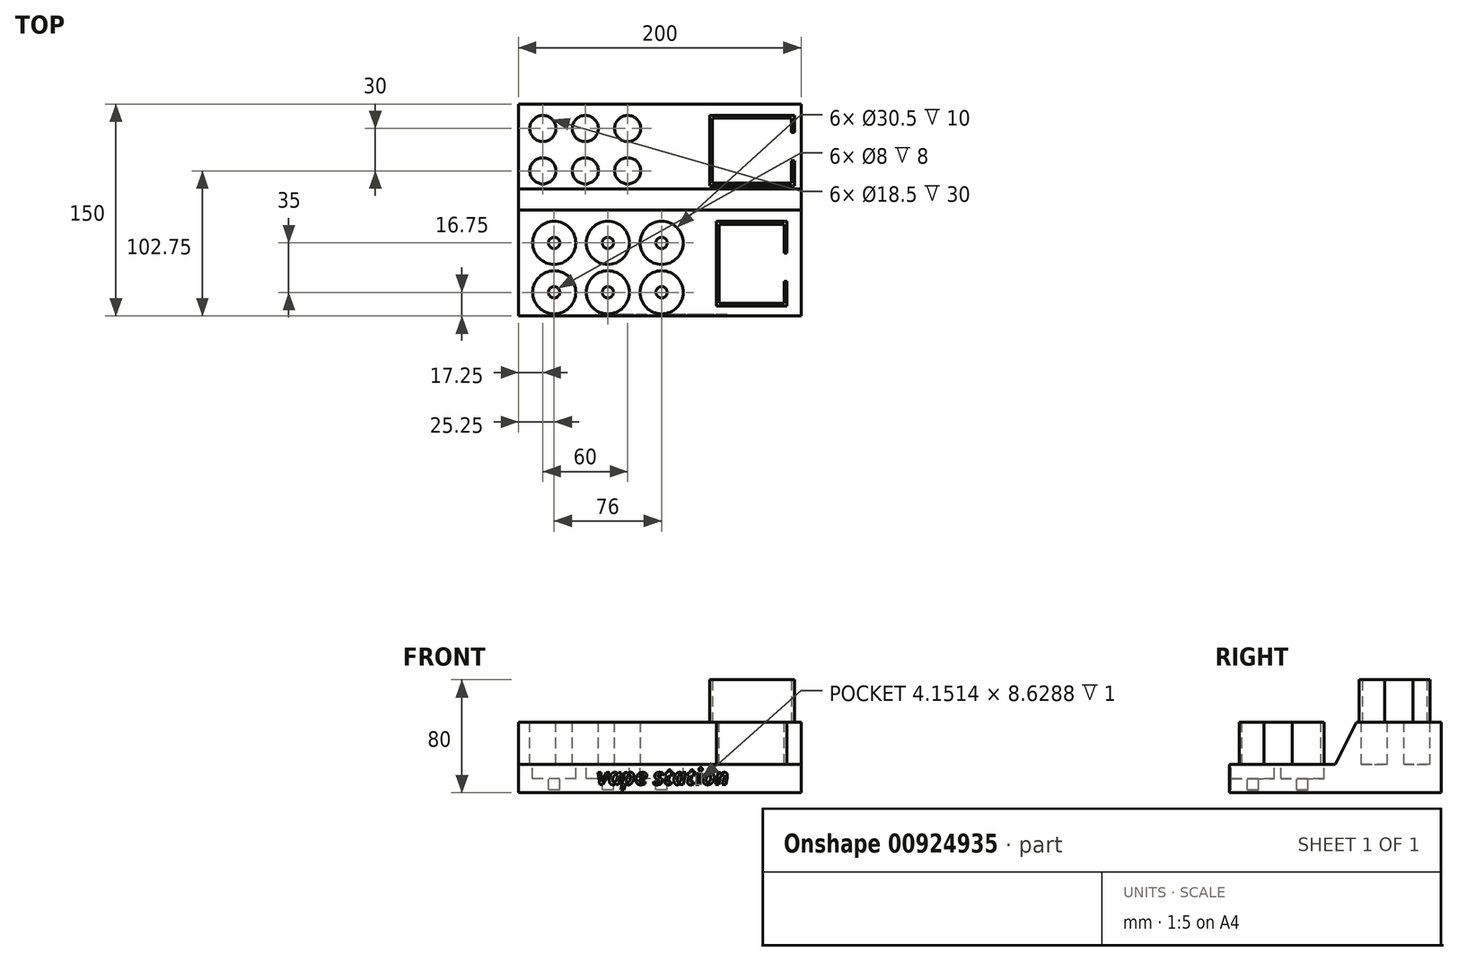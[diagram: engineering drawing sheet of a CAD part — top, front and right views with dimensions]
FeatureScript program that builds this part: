
annotation { "Feature Type Name" : "Feature", "Feature Type Description" : "" }
export const myFeature = defineFeature(function(context is Context, id is Id, definition is map)
    precondition{}
    {
        {
            var Q0;
            Q0=qCreatedBy(makeId("Top.planeOp"),FACE);
            var sketch = newSketch(context, id + "F0", { "sketchPlane" : qUnion([Q0])});
            skLineSegment(sketch, "E0.bottom", {"start": v(100, -75) * mm, "end": v(-100, -75) * mm});
            skLineSegment(sketch, "E0.top", {"start": v(100, 75) * mm, "end": v(-100, 75) * mm});
            skLineSegment(sketch, "E0.left", {"start": v(100, -75) * mm, "end": v(100, 75) * mm});
            skLineSegment(sketch, "E0.right", {"start": v(-100, -75) * mm, "end": v(-100, 75) * mm});
            skPoint(sketch, "E0.middle", {"position": v(0, 0) * mm});
            skSolve(sketch);
        }
        {
            var Q0;
            Q0=makeQuery(id+"F0.imprint","IMPRINT",FACE,{"disambiguationData":[TD([[makeQuery(id+"F0.imprint","IMPRINT",EDGE,{"derivedFrom":sQuery(id+"F0.wireOp",EDGE,"E0.bottom")}),-1.0]])]});
            extrude(context, id + "F1", {"entities" : qUnion([Q0]), "depth" : 20 * mm, "offsetDistance" : 25 * mm});
        }
        {
            var Q0;
            Q0=makeQuery(id+"F1.opExtrude","CAP_FACE",FACE,{"disambiguationData":[OSD([sQuery(id+"F0.wireOp",EDGE,"E0.bottom"),sQuery(id+"F0.wireOp",EDGE,"E0.top"),sQuery(id+"F0.wireOp",EDGE,"E0.left"),sQuery(id+"F0.wireOp",EDGE,"E0.right")])],"isStart":false});
            var sketch = newSketch(context, id + "F2", { "sketchPlane" : qUnion([Q0])});
            skLineSegment(sketch, "E1", {"start": v(-100, 0) * mm, "end": v(100, 0) * mm});
            skCircle(sketch, "E2", {"center": v(-74.75, -23.25) * mm, "radius": 15.25 * mm});
            skCircle(sketch, "E3", {"center": v(-74.75, -23.25) * mm, "radius": 4 * mm});
            skCircle(sketch, "E4.0.1.0", {"center": v(-74.75, -58.25) * mm, "radius": 4 * mm});
            skCircle(sketch, "E4.0.1.1", {"center": v(-74.75, -58.25) * mm, "radius": 15.25 * mm});
            skCircle(sketch, "E4.1.0.0", {"center": v(-36.75, -23.25) * mm, "radius": 4 * mm});
            skCircle(sketch, "E4.1.0.1", {"center": v(-36.75, -23.25) * mm, "radius": 15.25 * mm});
            skCircle(sketch, "E4.1.1.0", {"center": v(-36.75, -58.25) * mm, "radius": 4 * mm});
            skCircle(sketch, "E4.1.1.1", {"center": v(-36.75, -58.25) * mm, "radius": 15.25 * mm});
            skCircle(sketch, "E4.2.0.0", {"center": v(1.25, -23.25) * mm, "radius": 4 * mm});
            skCircle(sketch, "E4.2.0.1", {"center": v(1.25, -23.25) * mm, "radius": 15.25 * mm});
            skCircle(sketch, "E4.2.1.0", {"center": v(1.25, -58.25) * mm, "radius": 4 * mm});
            skCircle(sketch, "E4.2.1.1", {"center": v(1.25, -58.25) * mm, "radius": 15.25 * mm});
            skLineSegment(sketch, "E4.direction1", {"start": v(-74.75, -23.25) * mm, "end": v(-36.75, -23.25) * mm, "construction": true});
            skLineSegment(sketch, "E4.direction2", {"start": v(-74.75, -23.25) * mm, "end": v(-74.75, -58.25) * mm, "construction": true});
            skLineSegment(sketch, "E5.bottom", {"start": v(90, -8) * mm, "end": v(40, -8) * mm});
            skLineSegment(sketch, "E5.top", {"start": v(90, -68) * mm, "end": v(40, -68) * mm});
            skLineSegment(sketch, "E5.left", {"start": v(90, -8) * mm, "end": v(90, -68) * mm});
            skLineSegment(sketch, "E5.right", {"start": v(40, -8) * mm, "end": v(40, -68) * mm});
            skSolve(sketch);
        }
        {
            var Q0;
            Q0=makeQuery(id+"F2.imprint","IMPRINT",FACE,{"disambiguationData":[TD([[makeQuery(id+"F2.imprint","IMPRINT",EDGE,{"derivedFrom":sQuery(id+"F2.wireOp",EDGE,"E2")}),1.0]])]});
            var Q1;
            Q1=makeQuery(id+"F2.imprint","IMPRINT",FACE,{"disambiguationData":[TD([[makeQuery(id+"F2.imprint","IMPRINT",EDGE,{"derivedFrom":sQuery(id+"F2.wireOp",EDGE,"E4.1.0.0")}),-1.0]])]});
            var Q2;
            Q2=makeQuery(id+"F2.imprint","IMPRINT",FACE,{"disambiguationData":[TD([[makeQuery(id+"F2.imprint","IMPRINT",EDGE,{"derivedFrom":sQuery(id+"F2.wireOp",EDGE,"E4.2.0.0")}),-1.0]])]});
            var Q3;
            Q3=makeQuery(id+"F2.imprint","IMPRINT",FACE,{"disambiguationData":[TD([[makeQuery(id+"F2.imprint","IMPRINT",EDGE,{"derivedFrom":sQuery(id+"F2.wireOp",EDGE,"E4.2.1.0")}),-1.0]])]});
            var Q4;
            Q4=makeQuery(id+"F2.imprint","IMPRINT",FACE,{"disambiguationData":[TD([[makeQuery(id+"F2.imprint","IMPRINT",EDGE,{"derivedFrom":sQuery(id+"F2.wireOp",EDGE,"E4.1.1.0")}),-1.0]])]});
            var Q5;
            Q5=makeQuery(id+"F2.imprint","IMPRINT",FACE,{"disambiguationData":[TD([[makeQuery(id+"F2.imprint","IMPRINT",EDGE,{"derivedFrom":sQuery(id+"F2.wireOp",EDGE,"E4.0.1.0")}),-1.0]])]});
            extrude(context, id + "F3", {"entities" : qUnion([Q0, Q1, Q2, Q3, Q4, Q5]), "operationType" : NewBodyOperationType.REMOVE, "oppositeDirection" : true, "depth" : 10 * mm, "offsetDistance" : 25 * mm});
        }
        {
            var Q0;
            Q0=makeQuery(id+"F3.boolean.opBoolean","SPLIT",FACE,{"disambiguationData":[TD([makeQuery(id+"F3.opExtrude","SWEPT_FACE",FACE,{"disambiguationData":[OSD([sQuery(id+"F2.wireOp",EDGE,"E3")])]})])],"derivedFrom":makeQuery(id+"F1.opExtrude","CAP_FACE",FACE,{"disambiguationData":[OSD([sQuery(id+"F0.wireOp",EDGE,"E0.bottom"),sQuery(id+"F0.wireOp",EDGE,"E0.top"),sQuery(id+"F0.wireOp",EDGE,"E0.left"),sQuery(id+"F0.wireOp",EDGE,"E0.right")])],"isStart":false})});
            var Q1;
            Q1=makeQuery(id+"F3.boolean.opBoolean","SPLIT",FACE,{"disambiguationData":[TD([makeQuery(id+"F3.opExtrude","SWEPT_FACE",FACE,{"disambiguationData":[OSD([sQuery(id+"F2.wireOp",EDGE,"E4.1.0.0")])]})])],"derivedFrom":makeQuery(id+"F1.opExtrude","CAP_FACE",FACE,{"disambiguationData":[OSD([sQuery(id+"F0.wireOp",EDGE,"E0.bottom"),sQuery(id+"F0.wireOp",EDGE,"E0.top"),sQuery(id+"F0.wireOp",EDGE,"E0.left"),sQuery(id+"F0.wireOp",EDGE,"E0.right")])],"isStart":false})});
            var Q2;
            Q2=makeQuery(id+"F3.boolean.opBoolean","SPLIT",FACE,{"disambiguationData":[TD([makeQuery(id+"F3.opExtrude","SWEPT_FACE",FACE,{"disambiguationData":[OSD([sQuery(id+"F2.wireOp",EDGE,"E4.2.0.0")])]})])],"derivedFrom":makeQuery(id+"F1.opExtrude","CAP_FACE",FACE,{"disambiguationData":[OSD([sQuery(id+"F0.wireOp",EDGE,"E0.bottom"),sQuery(id+"F0.wireOp",EDGE,"E0.top"),sQuery(id+"F0.wireOp",EDGE,"E0.left"),sQuery(id+"F0.wireOp",EDGE,"E0.right")])],"isStart":false})});
            var Q3;
            Q3=makeQuery(id+"F3.boolean.opBoolean","SPLIT",FACE,{"disambiguationData":[TD([makeQuery(id+"F3.opExtrude","SWEPT_FACE",FACE,{"disambiguationData":[OSD([sQuery(id+"F2.wireOp",EDGE,"E4.2.1.0")])]})])],"derivedFrom":makeQuery(id+"F1.opExtrude","CAP_FACE",FACE,{"disambiguationData":[OSD([sQuery(id+"F0.wireOp",EDGE,"E0.bottom"),sQuery(id+"F0.wireOp",EDGE,"E0.top"),sQuery(id+"F0.wireOp",EDGE,"E0.left"),sQuery(id+"F0.wireOp",EDGE,"E0.right")])],"isStart":false})});
            var Q4;
            Q4=makeQuery(id+"F3.boolean.opBoolean","SPLIT",FACE,{"disambiguationData":[TD([makeQuery(id+"F3.opExtrude","SWEPT_FACE",FACE,{"disambiguationData":[OSD([sQuery(id+"F2.wireOp",EDGE,"E4.1.1.0")])]})])],"derivedFrom":makeQuery(id+"F1.opExtrude","CAP_FACE",FACE,{"disambiguationData":[OSD([sQuery(id+"F0.wireOp",EDGE,"E0.bottom"),sQuery(id+"F0.wireOp",EDGE,"E0.top"),sQuery(id+"F0.wireOp",EDGE,"E0.left"),sQuery(id+"F0.wireOp",EDGE,"E0.right")])],"isStart":false})});
            var Q5;
            Q5=makeQuery(id+"F3.boolean.opBoolean","SPLIT",FACE,{"disambiguationData":[TD([makeQuery(id+"F3.opExtrude","SWEPT_FACE",FACE,{"disambiguationData":[OSD([sQuery(id+"F2.wireOp",EDGE,"E4.0.1.0")])]})])],"derivedFrom":makeQuery(id+"F1.opExtrude","CAP_FACE",FACE,{"disambiguationData":[OSD([sQuery(id+"F0.wireOp",EDGE,"E0.bottom"),sQuery(id+"F0.wireOp",EDGE,"E0.top"),sQuery(id+"F0.wireOp",EDGE,"E0.left"),sQuery(id+"F0.wireOp",EDGE,"E0.right")])],"isStart":false})});
            extrude(context, id + "F4", {"entities" : qUnion([Q0, Q1, Q2, Q3, Q4, Q5]), "operationType" : NewBodyOperationType.REMOVE, "oppositeDirection" : true, "depth" : 18 * mm, "offsetDistance" : 25 * mm});
        }
        {
            var Q0;
            Q0=makeQuery(id+"F2.imprint","IMPRINT",FACE,{"disambiguationData":[TD([[makeQuery(id+"F2.imprint","IMPRINT",EDGE,{"derivedFrom":sQuery(id+"F2.wireOp",EDGE,"E5.bottom")}),1.0]])]});
            extrude(context, id + "F5", {"entities" : qUnion([Q0]), "operationType" : NewBodyOperationType.ADD, "depth" : 30 * mm, "offsetDistance" : 25 * mm});
        }
        {
            var Q0;
            Q0=makeQuery(id+"F5.opExtrude","SWEPT_FACE",FACE,{"disambiguationData":[OSD([sQuery(id+"F2.wireOp",EDGE,"E5.left")])]});
            var sketch = newSketch(context, id + "F6", { "sketchPlane" : qUnion([Q0])});
            skLineSegment(sketch, "E6.bottom", {"start": v(-30.38, 20) * mm, "end": v(-50.38, 20) * mm});
            skLineSegment(sketch, "E6.top", {"start": v(-30.38, 50) * mm, "end": v(-50.38, 50) * mm});
            skLineSegment(sketch, "E6.left", {"start": v(-30.38, 20) * mm, "end": v(-30.38, 50) * mm});
            skLineSegment(sketch, "E6.right", {"start": v(-50.38, 20) * mm, "end": v(-50.38, 50) * mm});
            skPoint(sketch, "E6.middle", {"position": v(-40.38, 35) * mm});
            skSolve(sketch);
        }
        {
            var Q0;
            Q0 = qSketchRegion(id + "F6", true);
            var Q1;
            Q1=makeQuery(id+"F5.opExtrude","SWEPT_FACE",FACE,{"disambiguationData":[OSD([sQuery(id+"F2.wireOp",EDGE,"E5.left")])]});
            extrude(context, id + "F7", {"entities" : qUnion([Q0]), "operationType" : NewBodyOperationType.REMOVE, "oppositeDirection" : true, "depth" : 2.5 * mm, "endBoundEntityFace" : qUnion([Q1]), "offsetDistance" : 25 * mm});
        }
        {
            var Q0;
            Q0=makeQuery(id+"F5.opExtrude","CAP_FACE",FACE,{"disambiguationData":[OSD([sQuery(id+"F2.wireOp",EDGE,"E5.bottom"),sQuery(id+"F2.wireOp",EDGE,"E5.top"),sQuery(id+"F2.wireOp",EDGE,"E5.left"),sQuery(id+"F2.wireOp",EDGE,"E5.right")])],"isStart":false});
            var sketch = newSketch(context, id + "F8", { "sketchPlane" : qUnion([Q0])});
            skLineSegment(sketch, "E7.bottom", {"start": v(88, -10) * mm, "end": v(42, -10) * mm});
            skLineSegment(sketch, "E7.top", {"start": v(88, -66) * mm, "end": v(42, -66) * mm});
            skLineSegment(sketch, "E7.left", {"start": v(88, -10) * mm, "end": v(88, -66) * mm});
            skLineSegment(sketch, "E7.right", {"start": v(42, -10) * mm, "end": v(42, -66) * mm});
            skPoint(sketch, "E7.middle", {"position": v(65, -38) * mm});
            skSolve(sketch);
        }
        {
            var Q0;
            {var subQ7=sQuery(id+"F8.wireOp",EDGE,"E7.bottom");Q0=makeQuery(id+"F8.imprint","IMPRINT",FACE,{"disambiguationData":[TD([[makeQuery(id+"F8.imprint","IMPRINT",EDGE,{"derivedFrom":subQ7}),1.0]])]});}
            var Q1;
            {var subQ0=sQuery(id+"F0.wireOp",EDGE,"E0.left");var subQ1=sQuery(id+"F0.wireOp",EDGE,"E0.top");var subQ2=sQuery(id+"F0.wireOp",EDGE,"E0.right");var subQ3=sQuery(id+"F0.wireOp",EDGE,"E0.bottom");Q1=makeQuery(id+"F3.boolean.opBoolean","SPLIT",FACE,{"disambiguationData":[TD([makeQuery(id+"F1.opExtrude","SWEPT_FACE",FACE,{"disambiguationData":[OSD([subQ3])]})])],"derivedFrom":makeQuery(id+"F1.opExtrude","CAP_FACE",FACE,{"disambiguationData":[OSD([subQ3,subQ1,subQ0,subQ2])],"isStart":false})});}
            extrude(context, id + "F9", {"entities" : qUnion([Q0]), "operationType" : NewBodyOperationType.REMOVE, "endBound" : BoundingType.UP_TO_SURFACE, "oppositeDirection" : true, "depth" : 40 * mm, "endBoundEntityFace" : qUnion([Q1]), "offsetDistance" : 25 * mm});
        }
        {
            var Q0;
            {var subQ0=sQuery(id+"F2.wireOp",EDGE,"E1");Q0=makeQuery(id+"F2.imprint","IMPRINT",FACE,{"disambiguationData":[TD([[makeQuery(id+"F2.imprint","IMPRINT",EDGE,{"derivedFrom":subQ0}),1.0]])]});}
            extrude(context, id + "F10", {"entities" : qUnion([Q0]), "operationType" : NewBodyOperationType.ADD, "depth" : 30 * mm, "offsetDistance" : 25 * mm});
        }
        {
            var Q0;
            Q0=makeQuery(id+"F10.opExtrude","CAP_FACE",FACE,{"disambiguationData":[OSD([sQuery(id+"F0.wireOp",EDGE,"E0.top"),sQuery(id+"F0.wireOp",EDGE,"E0.left"),sQuery(id+"F0.wireOp",EDGE,"E0.right"),sQuery(id+"F2.wireOp",EDGE,"E1")])],"isStart":false});
            var sketch = newSketch(context, id + "F11", { "sketchPlane" : qUnion([Q0])});
            skCircle(sketch, "E8", {"center": v(-82.75, 57.75) * mm, "radius": 9.25 * mm});
            skCircle(sketch, "E9.0.1.0", {"center": v(-82.75, 27.75) * mm, "radius": 9.25 * mm});
            skCircle(sketch, "E9.1.0.0", {"center": v(-52.75, 57.75) * mm, "radius": 9.25 * mm});
            skCircle(sketch, "E9.1.1.0", {"center": v(-52.75, 27.75) * mm, "radius": 9.25 * mm});
            skLineSegment(sketch, "E9.direction1", {"start": v(-82.75, 57.75) * mm, "end": v(-52.75, 57.75) * mm, "construction": true});
            skLineSegment(sketch, "E9.direction2", {"start": v(-82.75, 57.75) * mm, "end": v(-82.75, 27.75) * mm, "construction": true});
            skLineSegment(sketch, "E10.bottom", {"start": v(35.13, 67) * mm, "end": v(95.13, 67) * mm});
            skLineSegment(sketch, "E10.top", {"start": v(35.13, 17) * mm, "end": v(95.13, 17) * mm});
            skLineSegment(sketch, "E10.left", {"start": v(35.13, 67) * mm, "end": v(35.13, 17) * mm});
            skLineSegment(sketch, "E11.bottom", {"start": v(93.13, 19) * mm, "end": v(37.13, 19) * mm});
            skLineSegment(sketch, "E11.top", {"start": v(93.13, 65) * mm, "end": v(37.13, 65) * mm});
            skLineSegment(sketch, "E11.right", {"start": v(37.13, 19) * mm, "end": v(37.13, 65) * mm});
            skPoint(sketch, "E11.middle", {"position": v(65.13, 42) * mm});
            skLineSegment(sketch, "E12", {"start": v(93.13, 55) * mm, "end": v(95.13, 55) * mm});
            skLineSegment(sketch, "E13", {"start": v(93.13, 35) * mm, "end": v(95.13, 35) * mm});
            skLineSegment(sketch, "E14", {"start": v(93.13, 65) * mm, "end": v(93.13, 55) * mm});
            skLineSegment(sketch, "E15", {"start": v(95.13, 67) * mm, "end": v(95.13, 55) * mm});
            skLineSegment(sketch, "E16", {"start": v(93.13, 35) * mm, "end": v(93.13, 19) * mm});
            skLineSegment(sketch, "E17", {"start": v(95.13, 35) * mm, "end": v(95.13, 17) * mm});
            skLineSegment(sketch, "E18", {"start": v(30.13, 89.64) * mm, "end": v(30.13, -104.1) * mm, "construction": true});
            skCircle(sketch, "E19.0.2.0", {"center": v(-22.75, 57.75) * mm, "radius": 9.25 * mm});
            skCircle(sketch, "E19.0.2.1", {"center": v(-22.75, 27.75) * mm, "radius": 9.25 * mm});
            skSolve(sketch);
        }
        {
            var Q0;
            Q0=makeQuery(id+"F11.imprint","IMPRINT",FACE,{"disambiguationData":[TD([[makeQuery(id+"F11.imprint","IMPRINT",EDGE,{"derivedFrom":sQuery(id+"F11.wireOp",EDGE,"E8")}),1.0]])]});
            var Q1;
            Q1=makeQuery(id+"F11.imprint","IMPRINT",FACE,{"disambiguationData":[TD([[makeQuery(id+"F11.imprint","IMPRINT",EDGE,{"derivedFrom":sQuery(id+"F11.wireOp",EDGE,"E9.1.0.0")}),1.0]])]});
            var Q2;
            Q2=makeQuery(id+"F11.imprint","IMPRINT",FACE,{"disambiguationData":[TD([[makeQuery(id+"F11.imprint","IMPRINT",EDGE,{"derivedFrom":sQuery(id+"F11.wireOp",EDGE,"E9.1.1.0")}),1.0]])]});
            var Q3;
            Q3=makeQuery(id+"F11.imprint","IMPRINT",FACE,{"disambiguationData":[TD([[makeQuery(id+"F11.imprint","IMPRINT",EDGE,{"derivedFrom":sQuery(id+"F11.wireOp",EDGE,"E9.0.1.0")}),1.0]])]});
            var Q4;
            Q4=makeQuery(id+"F11.imprint","IMPRINT",FACE,{"disambiguationData":[TD([[makeQuery(id+"F11.imprint","IMPRINT",EDGE,{"derivedFrom":sQuery(id+"F11.wireOp",EDGE,"E19.0.2.1")}),1.0]])]});
            var Q5;
            Q5=makeQuery(id+"F11.imprint","IMPRINT",FACE,{"disambiguationData":[TD([[makeQuery(id+"F11.imprint","IMPRINT",EDGE,{"derivedFrom":sQuery(id+"F11.wireOp",EDGE,"E19.0.2.0")}),1.0]])]});
            extrude(context, id + "F12", {"entities" : qUnion([Q0, Q1, Q2, Q3, Q4, Q5]), "operationType" : NewBodyOperationType.REMOVE, "oppositeDirection" : true, "depth" : 30 * mm, "offsetDistance" : 25 * mm});
        }
        {
            var Q0;
            Q0=makeQuery(id+"F11.imprint","IMPRINT",FACE,{"disambiguationData":[TD([[makeQuery(id+"F11.imprint","IMPRINT",EDGE,{"derivedFrom":sQuery(id+"F11.wireOp",EDGE,"E10.bottom")}),-1.0]])]});
            extrude(context, id + "F13", {"entities" : qUnion([Q0]), "operationType" : NewBodyOperationType.ADD, "depth" : 30 * mm, "offsetDistance" : 25 * mm});
        }
        {
            var Q0;
            Q0=makeQuery(id+"F1.opExtrude","SWEPT_FACE",FACE,{"disambiguationData":[OSD([sQuery(id+"F0.wireOp",EDGE,"E0.bottom")])]});
            var sketch = newSketch(context, id + "F14", { "sketchPlane" : qUnion([Q0])});
            skText(sketch, "E20", { "text": "vape station", "fontName": "OpenSans-BoldItalic.ttf"});
            const initialGuessF14  = {"E20": [-0.04453, 0.00575, 1, 0, 0.01138]};
            skSetInitialGuess(sketch, initialGuessF14);
            skSolve(sketch);
        }
        {
            var Q0;
            Q0 = qSketchRegion(id + "F14", true);
            extrude(context, id + "F15", {"entities" : qUnion([Q0]), "operationType" : NewBodyOperationType.REMOVE, "oppositeDirection" : true, "depth" : 1 * mm, "offsetDistance" : 25 * mm});
        }
        {
            var Q0;
            {var subQ0=sQuery(id+"F0.wireOp",EDGE,"E0.right");Q0=makeQuery(id+"F10.boolean.opBoolean","MERGE",FACE,{"derivedFrom":[makeQuery(id+"F1.opExtrude","SWEPT_FACE",FACE,{"disambiguationData":[OSD([subQ0])]}),makeQuery(id+"F10.opExtrude","SWEPT_FACE",FACE,{"disambiguationData":[OSD([subQ0])]})]});}
            var sketch = newSketch(context, id + "F16", { "sketchPlane" : qUnion([Q0])});
            skLineSegment(sketch, "E21", {"start": v(-16.71, 50) * mm, "end": v(-16.71, -7.64) * mm, "construction": true});
            skLineSegment(sketch, "E22.bottom", {"start": v(-14.96, 50) * mm, "end": v(0.04, 50) * mm});
            skLineSegment(sketch, "E22.right", {"start": v(0.04, 50) * mm, "end": v(0.04, 20) * mm});
            skPoint(sketch, "E22.middle", {"position": v(-7.46, 35) * mm});
            skLineSegment(sketch, "E23", {"start": v(-14.96, 50) * mm, "end": v(0.04, 20) * mm});
            skLineSegment(sketch, "E24", {"start": v(14.04, 14.69) * mm, "end": v(-61.91, 14.69) * mm, "construction": true});
            skSolve(sketch);
        }
        {
            var Q0;
            {var subQ0=sQuery(id+"F16.wireOp",EDGE,"E22.bottom");var subQ1=sQuery(id+"F0.wireOp",EDGE,"E0.right");var subQ4=sQuery(id+"F16.wireOp",EDGE,"E23");var subQ5=makeQuery(id+"F16.imprint","INTERSECT",VERTEX,{"derivedFrom":[makeQuery(id+"F10.opExtrude","CAP_EDGE",EDGE,{"disambiguationData":[OSD([subQ1])],"isStart":false}),subQ0,subQ4]});Q0=makeQuery(id+"F16.imprint","IMPRINT",FACE,{"disambiguationData":[TD([[makeQuery(id+"F16.imprint","IMPRINT",EDGE,{"disambiguationData":[TD([[subQ5,1.0]])],"derivedFrom":subQ0}),1.0]])]});}
            extrude(context, id + "F17", {"entities" : qUnion([Q0]), "operationType" : NewBodyOperationType.REMOVE, "endBound" : BoundingType.UP_TO_NEXT, "oppositeDirection" : true, "depth" : 25 * mm, "offsetDistance" : 25 * mm});
        }
    });
